# Revit family: BuzziZepp Light
name_source: partatom
category: Lighting Fixtures
revit_build: Autodesk Revit 2018 (Build: 20190510_1515(x64)
units: mm (PartAtom-declared; Revit-internal decimal feet)

## family parameters
Always vertical = Yes
Cut with Voids When Loaded = No
Host = Ceiling
Light Source = Yes
OmniClass Number = 23.80.70.11
OmniClass Title = Luminaries for Internal Lighting
Part Type = Normal
Room Calculation Point = No
Round Connector Dimension = Use Diameter
Shared = No

## types (6) — shared parameters
Color Filter = 16777215
Dimming Lamp Color Temperature Shift = <None>
Light Source Symbol Size = 2' - 0"

## per-type parameters (varying)
| type | 5 Fixtures | Light Type | Medium Panel | Panel Type | Small Panel |
| Light Medium- Quintet Globe | Yes | Light Bar : 5 Fixture Globe | Yes | Acoustic Panel : Medium | No |
| Light Medium- Quintet Spot | Yes | Light Bar : 5 Fixture Spot | Yes | Acoustic Panel : Medium | No |
| Light Small- Quintet Globe | Yes | Light Bar : 5 Fixture Globe | No | Acoustic Panel : Small | Yes |
| Light Small- Quintet Spot | Yes | Light Bar : 5 Fixture Spot | No | Acoustic Panel : Small | Yes |
| Light Small- Trio Globe | No | Light Bar : 3 Fixture Globe | No | Acoustic Panel : Small | Yes |
| Light Small- Trio Spot | No | Light Bar : 3 Fixture Spot | No | Acoustic Panel : Small | Yes |

## geometry (parser evidence)
native form markers: Sweep x10
no freeform markers — native parametric forms only
